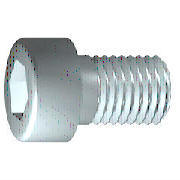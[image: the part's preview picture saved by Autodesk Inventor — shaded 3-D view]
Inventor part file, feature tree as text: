
AUTODESK INVENTOR PART (.ipt)
format: ipt  version: 2024 (Build 280153000, 153)  size: 188,928 bytes
history: native  units: mm (DEFAULTED — no unit token found)
features: extrude x1, plane x1, fillet x1
ambient origin geometry x7: Origin, YZ Plane, XY Plane, X Axis, Y Axis, Z Axis, Center Point
bodies: Solid1 (feature_tree), Body (feature_tree)
feature tree (3):
  extrude  "Slot"  Depth=9.0mm
  plane  "Work Plane1"
  fillet  "Fillet2"  Radius=0.24548mm
